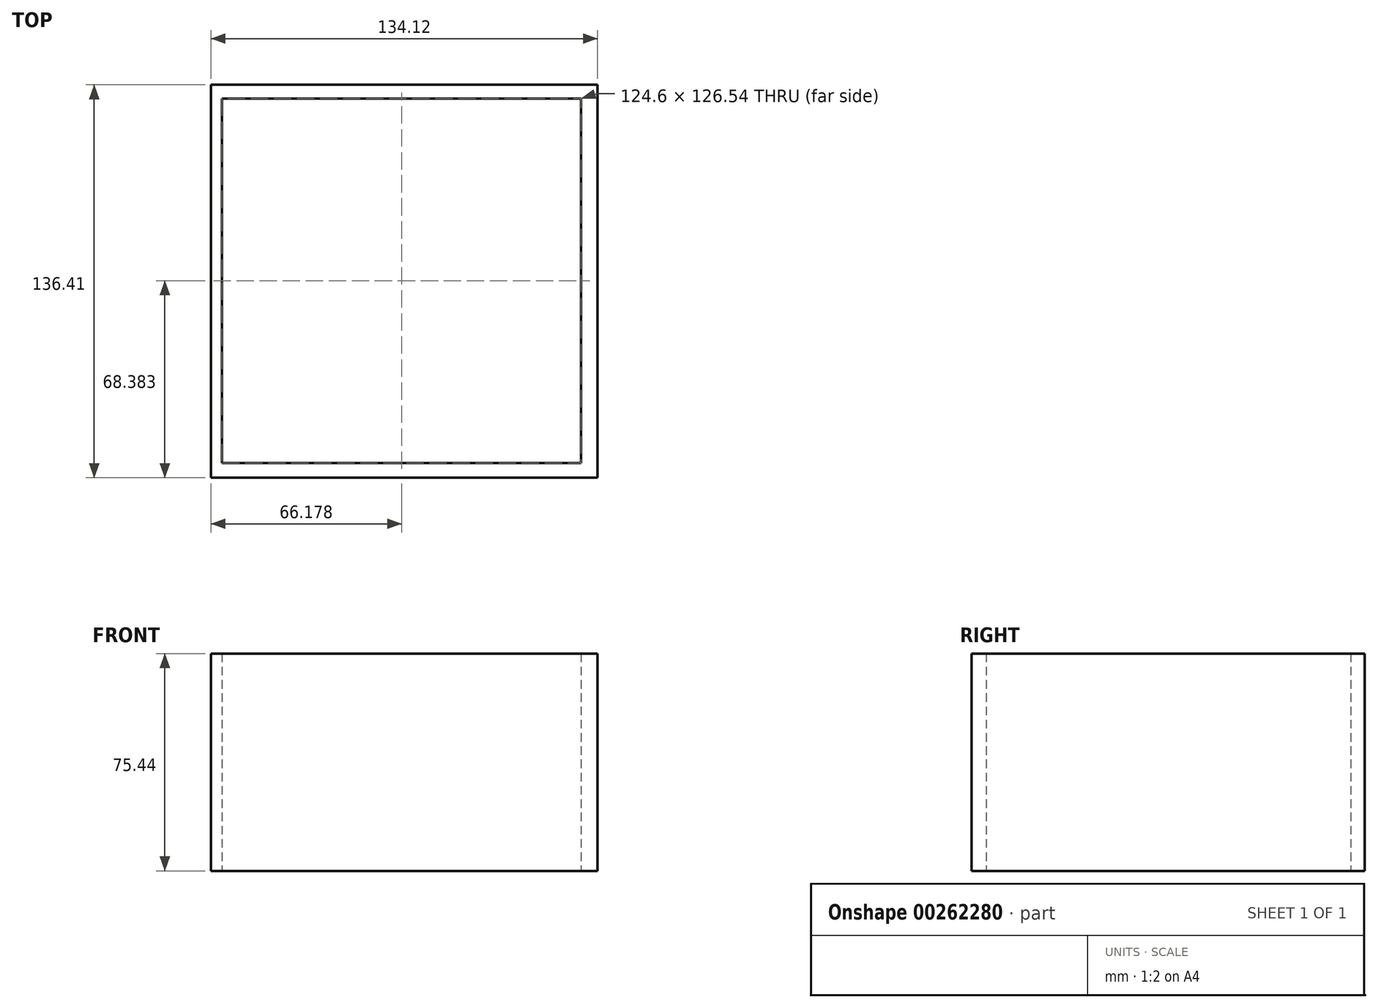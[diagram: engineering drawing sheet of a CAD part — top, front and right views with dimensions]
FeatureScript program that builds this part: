
annotation { "Feature Type Name" : "Feature", "Feature Type Description" : "" }
export const myFeature = defineFeature(function(context is Context, id is Id, definition is map)
    precondition{}
    {
        {
            var Q0;
            Q0=qCreatedBy(makeId("Top.planeOp"),FACE);
            var sketch = newSketch(context, id + "F0", { "sketchPlane" : qUnion([Q0])});
            skLineSegment(sketch, "E0.bottom", {"start": v(-67.5, 66.97) * mm, "end": v(66.62, 66.97) * mm});
            skLineSegment(sketch, "E0.top", {"start": v(-67.5, -69.44) * mm, "end": v(66.62, -69.44) * mm});
            skLineSegment(sketch, "E0.left", {"start": v(-67.5, 66.97) * mm, "end": v(-67.5, -69.44) * mm});
            skLineSegment(sketch, "E0.right", {"start": v(66.62, 66.97) * mm, "end": v(66.62, -69.44) * mm});
            skLineSegment(sketch, "E1.bottom", {"start": v(-63.62, 62.21) * mm, "end": v(60.98, 62.21) * mm});
            skLineSegment(sketch, "E1.top", {"start": v(-63.62, -64.33) * mm, "end": v(60.98, -64.33) * mm});
            skLineSegment(sketch, "E1.left", {"start": v(-63.62, 62.21) * mm, "end": v(-63.62, -64.33) * mm});
            skLineSegment(sketch, "E1.right", {"start": v(60.98, 62.21) * mm, "end": v(60.98, -64.33) * mm});
            skSolve(sketch);
        }
        {
            var Q0;
            Q0=makeQuery(id+"F0.imprint","IMPRINT",FACE,{"disambiguationData":[TD([[makeQuery(id+"F0.imprint","IMPRINT",EDGE,{"derivedFrom":sQuery(id+"F0.wireOp",EDGE,"E0.bottom")}),-1.0]])]});
            extrude(context, id + "F1", {"entities" : qUnion([Q0]), "depth" : 75.44 * mm});
        }
    });
